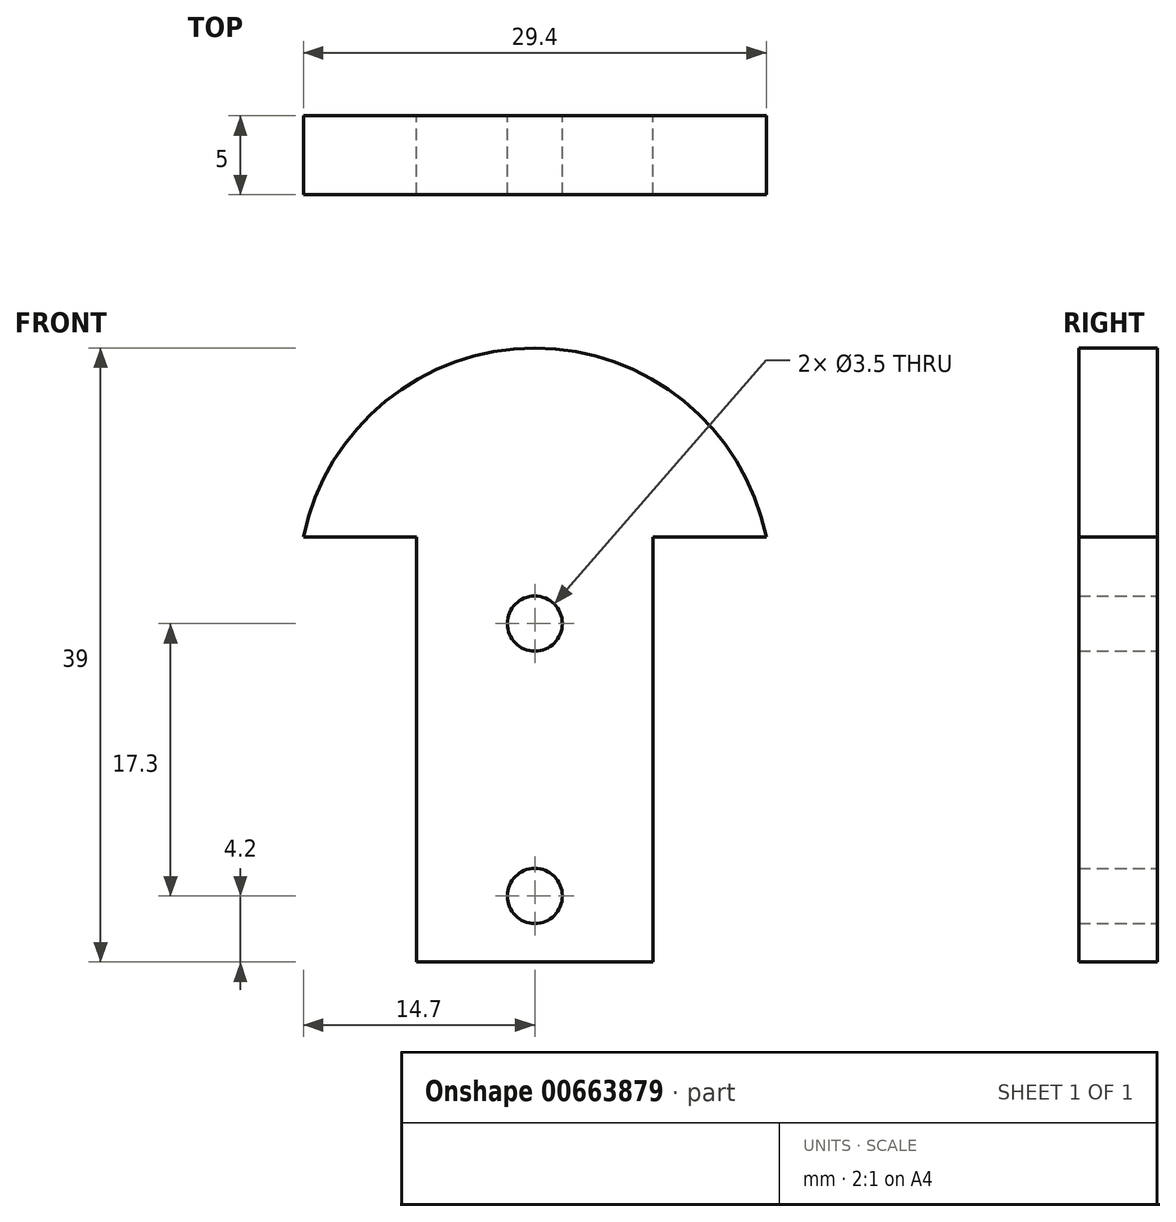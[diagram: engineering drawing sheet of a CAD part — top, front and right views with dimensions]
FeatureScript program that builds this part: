
annotation { "Feature Type Name" : "Feature", "Feature Type Description" : "" }
export const myFeature = defineFeature(function(context is Context, id is Id, definition is map)
    precondition{}
    {
        {
            var Q0;
            Q0=qCreatedBy(makeId("Front.planeOp"),FACE);
            var sketch = newSketch(context, id + "F0", { "sketchPlane" : qUnion([Q0])});
            skLineSegment(sketch, "E0.top", {"start": v(7.5, -13.5) * mm, "end": v(-7.5, -13.5) * mm});
            skLineSegment(sketch, "E0.left", {"start": v(7.5, 13.5) * mm, "end": v(7.5, -13.5) * mm});
            skLineSegment(sketch, "E0.right", {"start": v(-7.5, 13.5) * mm, "end": v(-7.5, -13.5) * mm});
            skPoint(sketch, "E0.middle", {"position": v(0, 0) * mm});
            skArc(sketch, "E1", {"start": v(14.7, 13.5) * mm, "mid": v(0, 25.5) * mm, "end": v(-14.7, 13.5) * mm});
            skLineSegment(sketch, "E2", {"start": v(-14.7, 13.5) * mm, "end": v(-7.5, 13.5) * mm});
            skLineSegment(sketch, "E3", {"start": v(7.5, 13.5) * mm, "end": v(14.7, 13.5) * mm});
            skCircle(sketch, "E4", {"center": v(0, -9.3) * mm, "radius": 1.75 * mm});
            skCircle(sketch, "E5", {"center": v(0, 8) * mm, "radius": 1.75 * mm});
            skSolve(sketch);
        }
        {
            var Q0;
            Q0 = qSketchRegion(id + "F0", true);
            extrude(context, id + "F1", {"entities" : qUnion([Q0]), "depth" : 5 * mm, "offsetDistance" : 25 * mm});
        }
    });
